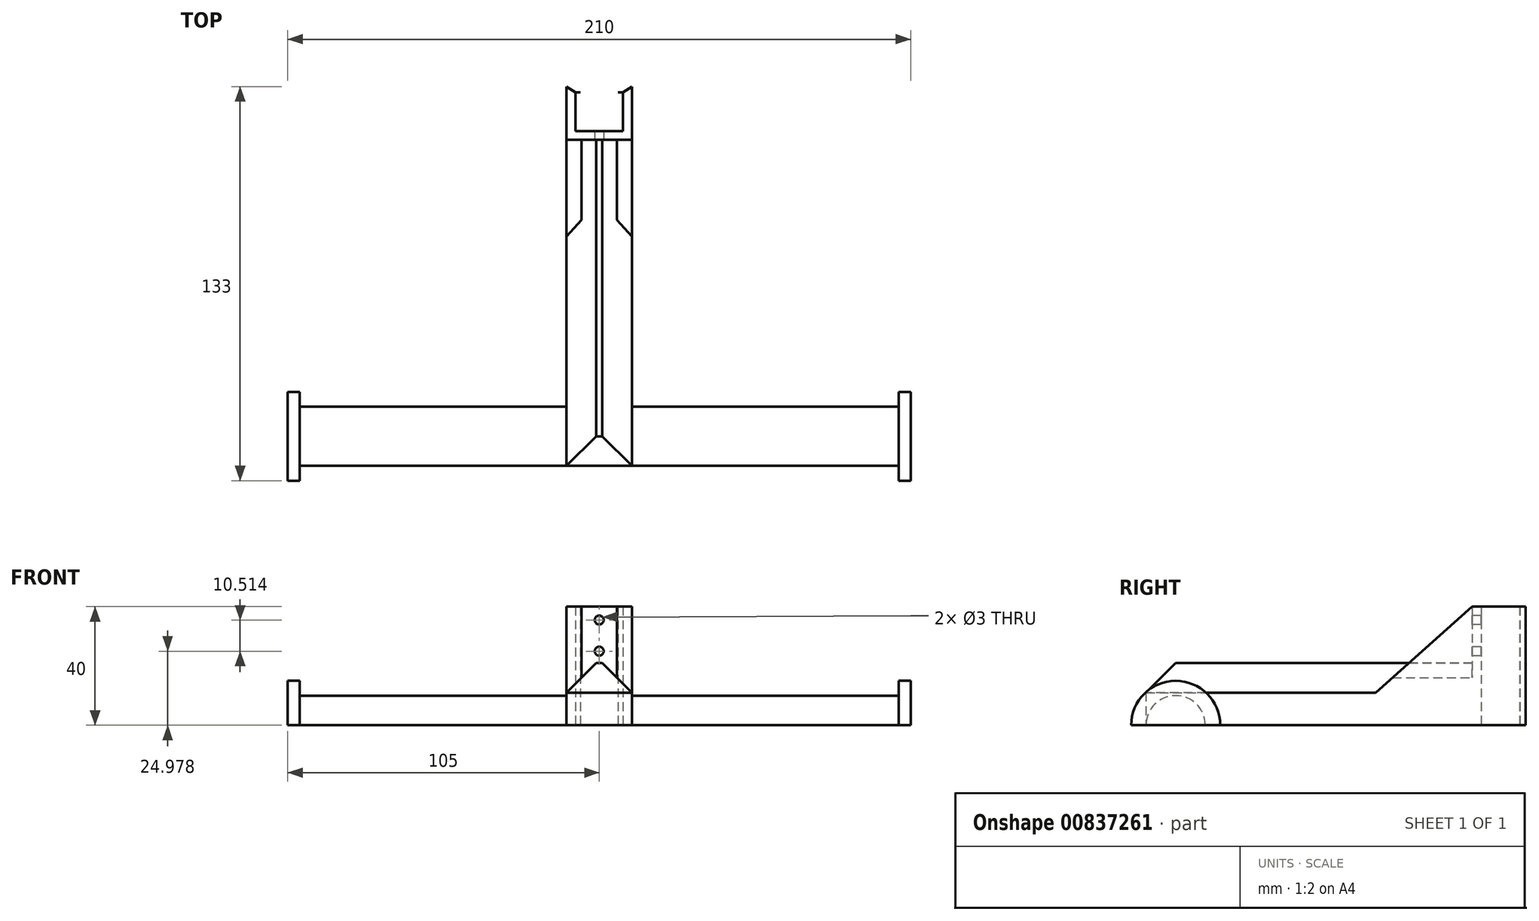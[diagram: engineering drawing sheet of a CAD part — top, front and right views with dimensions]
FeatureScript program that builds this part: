
annotation { "Feature Type Name" : "Feature", "Feature Type Description" : "" }
export const myFeature = defineFeature(function(context is Context, id is Id, definition is map)
    precondition{}
    {
        {
            var Q0;
            Q0=qCreatedBy(makeId("Front.planeOp"),FACE);
            var sketch = newSketch(context, id + "F0", { "sketchPlane" : qUnion([Q0])});
            skLineSegment(sketch, "E0.bottom", {"start": v(8, 7.5) * mm, "end": v(-8, 7.5) * mm});
            skLineSegment(sketch, "E0.top", {"start": v(8, -7.5) * mm, "end": v(-8, -7.5) * mm});
            skLineSegment(sketch, "E0.left", {"start": v(8, 7.5) * mm, "end": v(8, -7.5) * mm});
            skLineSegment(sketch, "E0.right", {"start": v(-8, 7.5) * mm, "end": v(-8, -7.5) * mm});
            skPoint(sketch, "E0.middle", {"position": v(0, 0) * mm});
            skLineSegment(sketch, "E1", {"start": v(8, 5.5) * mm, "end": v(6.3, 5.5) * mm});
            skLineSegment(sketch, "E2", {"start": v(6.3, 5.5) * mm, "end": v(8, 5.53) * mm});
            skLineSegment(sketch, "E3.0", {"start": v(11, 10.5) * mm, "end": v(-11, 10.5) * mm});
            skLineSegment(sketch, "E3.1", {"start": v(11, 10.5) * mm, "end": v(11, -10.5) * mm});
            skLineSegment(sketch, "E3.2", {"start": v(11, -10.5) * mm, "end": v(-11, -10.5) * mm});
            skLineSegment(sketch, "E3.3", {"start": v(-11, 10.5) * mm, "end": v(-11, -10.5) * mm});
            skLineSegment(sketch, "E4.MirrorCS", {"start": v(-6.3, 5.5) * mm, "end": v(-8, 5.53) * mm});
            skLineSegment(sketch, "E5.MirrorCS", {"start": v(-8, 5.5) * mm, "end": v(-6.3, 5.5) * mm});
            skLineSegment(sketch, "E6", {"start": v(8, 7.5) * mm, "end": v(11, 7.5) * mm});
            skLineSegment(sketch, "E7.MirrorCS", {"start": v(-8, 7.5) * mm, "end": v(-11, 7.5) * mm});
            skLineSegment(sketch, "E8", {"start": v(8, 5.53) * mm, "end": v(11, 7.5) * mm});
            skLineSegment(sketch, "E9.MirrorCS", {"start": v(-8, 5.53) * mm, "end": v(-11, 7.5) * mm});
            skSolve(sketch);
        }
        {
            var Q0;
            {var subQ1=sQuery(id+"F0.wireOp",EDGE,"E0.top");Q0=makeQuery(id+"F0.imprint","IMPRINT",FACE,{"disambiguationData":[TD([[makeQuery(id+"F0.imprint","IMPRINT",EDGE,{"derivedFrom":subQ1}),1.0]])]});}
            var Q1;
            {var subQ0=sQuery(id+"F0.wireOp",EDGE,"E4.MirrorCS");Q1=makeQuery(id+"F0.imprint","IMPRINT",FACE,{"disambiguationData":[TD([[makeQuery(id+"F0.imprint","IMPRINT",EDGE,{"derivedFrom":subQ0}),1.0]])]});}
            var Q2;
            {var subQ0=sQuery(id+"F0.wireOp",EDGE,"E1");Q2=makeQuery(id+"F0.imprint","IMPRINT",FACE,{"disambiguationData":[TD([[makeQuery(id+"F0.imprint","IMPRINT",EDGE,{"derivedFrom":subQ0}),-1.0]])]});}
            extrude(context, id + "F1", {"entities" : qUnion([Q0, Q1, Q2]), "depth" : 40 * mm, "offsetDistance" : 25 * mm});
        }
        {
            var Q0;
            Q0=makeQuery(id+"F1.opExtrude","SWEPT_FACE",FACE,{"disambiguationData":[OSD([sQuery(id+"F0.wireOp",EDGE,"E3.2")])]});
            var sketch = newSketch(context, id + "F2", { "sketchPlane" : qUnion([Q0])});
            skLineSegment(sketch, "E10", {"start": v(-11, 21) * mm, "end": v(11, 21) * mm});
            skSolve(sketch);
        }
        {
            var Q0;
            {var subQ0=sQuery(id+"F2.wireOp",EDGE,"E10");Q0=makeQuery(id+"F2.imprint","IMPRINT",FACE,{"disambiguationData":[TD([[makeQuery(id+"F2.imprint","IMPRINT",EDGE,{"derivedFrom":subQ0}),-1.0]])]});}
            extrude(context, id + "F3", {"entities" : qUnion([Q0]), "operationType" : NewBodyOperationType.ADD, "depth" : 110 * mm, "offsetDistance" : 25 * mm});
        }
        {
            var Q0;
            {var subQ0=sQuery(id+"F0.wireOp",EDGE,"E3.3");Q0=makeQuery(id+"F3.boolean.opBoolean","MERGE",FACE,{"derivedFrom":[makeQuery(id+"F1.opExtrude","SWEPT_FACE",FACE,{"disambiguationData":[OSD([subQ0])]}),makeQuery(id+"F3.opExtrude","SWEPT_FACE",FACE,{"disambiguationData":[OSD([sQuery(id+"F0.wireOp",EDGE,"E3.2"),subQ0])]})]});}
            var sketch = newSketch(context, id + "F4", { "sketchPlane" : qUnion([Q0])});
            skLineSegment(sketch, "E11", {"start": v(40, -10.5) * mm, "end": v(21, -31.83) * mm});
            skSolve(sketch);
        }
        {
            var Q0;
            {var subQ0=sQuery(id+"F4.wireOp",EDGE,"E11");Q0=makeQuery(id+"F4.imprint","IMPRINT",FACE,{"disambiguationData":[TD([[makeQuery(id+"F4.imprint","IMPRINT",EDGE,{"derivedFrom":subQ0}),-1.0]])]});}
            extrude(context, id + "F5", {"entities" : qUnion([Q0]), "operationType" : NewBodyOperationType.ADD, "depth" : -5 * mm, "offsetDistance" : 25 * mm});
        }
        {
            var Q0;
            Q0=makeQuery(id+"F1.opExtrude","SWEPT_BODY",BODY,{"disambiguationData":[OSD([sQuery(id+"F0.wireOp",EDGE,"E0.top"),sQuery(id+"F0.wireOp",EDGE,"E0.left"),sQuery(id+"F0.wireOp",EDGE,"E0.right"),sQuery(id+"F0.wireOp",EDGE,"E1"),sQuery(id+"F0.wireOp",EDGE,"E2"),sQuery(id+"F0.wireOp",EDGE,"E3.1"),sQuery(id+"F0.wireOp",EDGE,"E3.2"),sQuery(id+"F0.wireOp",EDGE,"E3.3"),sQuery(id+"F0.wireOp",EDGE,"E4.MirrorCS"),sQuery(id+"F0.wireOp",EDGE,"E5.MirrorCS"),sQuery(id+"F0.wireOp",EDGE,"E8"),sQuery(id+"F0.wireOp",EDGE,"E9.MirrorCS")])]});
            var Q1;
            Q1=qCreatedBy(makeId("Right.planeOp"),FACE);
            mirror(context, id + "F6", {"operationType" : NewBodyOperationType.ADD, "entities" : qUnion([Q0]), "mirrorPlane" : qUnion([Q1])});
        }
        {
            var Q0;
            Q0=makeQuery(id+"F3.opExtrude","SWEPT_EDGE",EDGE,{"disambiguationData":[OSD([sQuery(id+"F0.wireOp",EDGE,"E3.2"),sQuery(id+"F0.wireOp",EDGE,"E3.3"),sQuery(id+"F2.wireOp",EDGE,"E10")])]});
            var Q1;
            Q1=makeQuery(id+"F3.opExtrude","CAP_EDGE",EDGE,{"disambiguationData":[OSD([sQuery(id+"F2.wireOp",EDGE,"E10")])],"isStart":false});
            var Q2;
            Q2=makeQuery(id+"F3.opExtrude","SWEPT_EDGE",EDGE,{"disambiguationData":[OSD([sQuery(id+"F0.wireOp",EDGE,"E3.1"),sQuery(id+"F0.wireOp",EDGE,"E3.2"),sQuery(id+"F2.wireOp",EDGE,"E10")])]});
            chamfer(context, id + "F7", {"entities" : qUnion([Q0, Q1, Q2]), "width" : 10 * mm, "tangentPropagation" : true});
        }
        {
            var Q0;
            {var subQ0=sQuery(id+"F0.wireOp",EDGE,"E3.3");var subQ1=sQuery(id+"F0.wireOp",EDGE,"E3.2");Q0=makeQuery(id+"F5.boolean.opBoolean","MERGE",FACE,{"derivedFrom":[makeQuery(id+"F3.boolean.opBoolean","MERGE",FACE,{"derivedFrom":[makeQuery(id+"F1.opExtrude","SWEPT_FACE",FACE,{"disambiguationData":[OSD([subQ0])]}),makeQuery(id+"F3.opExtrude","SWEPT_FACE",FACE,{"disambiguationData":[OSD([subQ1,subQ0])]})]}),makeQuery(id+"F5.opExtrude","CAP_FACE",FACE,{"disambiguationData":[OSD([subQ1,subQ0,sQuery(id+"F2.wireOp",EDGE,"E10"),sQuery(id+"F4.wireOp",EDGE,"E11")])],"isStart":true})]});}
            var sketch = newSketch(context, id + "F8", { "sketchPlane" : qUnion([Q0])});
            skPoint(sketch, "E12", {"position": v(0, -110.5) * mm});
            skPoint(sketch, "E13", {"position": v(0, -120.5) * mm});
            skCircle(sketch, "E14", {"center": v(0, -110.5) * mm, "radius": 10 * mm});
            skPoint(sketch, "E15", {"position": v(0, -100.5) * mm});
            skSolve(sketch);
        }
        {
            var Q0;
            {var subQ0=sQuery(id+"F8.wireOp",EDGE,"E14");var subQ1=sQuery(id+"F0.wireOp",EDGE,"E3.3");var subQ2=sQuery(id+"F0.wireOp",EDGE,"E3.2");var subQ3=makeQuery(id+"F3.boolean.opBoolean","MERGE",EDGE,{"derivedFrom":[makeQuery(id+"F1.opExtrude","CAP_EDGE",EDGE,{"disambiguationData":[OSD([subQ1])],"isStart":true}),makeQuery(id+"F3.opExtrude","SWEPT_EDGE",EDGE,{"disambiguationData":[OSD([subQ2,subQ1])]})]});var subQ5=makeQuery(id+"F8.imprint","INTERSECT",VERTEX,{"derivedFrom":[subQ3,subQ0]});Q0=makeQuery(id+"F8.imprint","IMPRINT",FACE,{"disambiguationData":[TD([[makeQuery(id+"F8.imprint","IMPRINT",EDGE,{"disambiguationData":[TD([[subQ5,1.0]])],"derivedFrom":subQ0}),1.0]])]});}
            extrude(context, id + "F9", {"entities" : qUnion([Q0]), "operationType" : NewBodyOperationType.ADD, "depth" : 90 * mm, "offsetDistance" : 25 * mm});
        }
        {
            var Q0;
            Q0=makeQuery(id+"F9.opExtrude","CAP_FACE",FACE,{"disambiguationData":[OSD([sQuery(id+"F0.wireOp",EDGE,"E3.2"),sQuery(id+"F0.wireOp",EDGE,"E3.3"),sQuery(id+"F8.wireOp",EDGE,"E14")])],"isStart":false});
            var sketch = newSketch(context, id + "F10", { "sketchPlane" : qUnion([Q0])});
            skCircle(sketch, "E16", {"center": v(0, -110.5) * mm, "radius": 15 * mm});
            skPoint(sketch, "E17", {"position": v(0, -125.5) * mm});
            skLineSegment(sketch, "E18", {"start": v(0, -95.5) * mm, "end": v(0, -120.5) * mm});
            skLineSegment(sketch, "E19", {"start": v(0, -95.5) * mm, "end": v(0, -125.5) * mm});
            skSolve(sketch);
        }
        {
            var Q0;
            {var subQ4=makeQuery(id+"F9.opExtrude","CAP_EDGE",EDGE,{"disambiguationData":[OSD([sQuery(id+"F8.wireOp",EDGE,"E14")])],"isStart":false});Q0=makeQuery(id+"F10.imprint","IMPRINT",FACE,{"disambiguationData":[TD([[makeQuery(id+"F10.imprint","IMPRINT",EDGE,{"derivedFrom":subQ4}),-1.0]])]});}
            var Q1;
            {var subQ1=makeQuery(id+"F9.opExtrude","CAP_EDGE",EDGE,{"disambiguationData":[OSD([sQuery(id+"F8.wireOp",EDGE,"E14")])],"isStart":false});Q1=makeQuery(id+"F10.imprint","IMPRINT",FACE,{"disambiguationData":[TD([[makeQuery(id+"F10.imprint","IMPRINT",EDGE,{"derivedFrom":subQ1}),1.0]])]});}
            extrude(context, id + "F11", {"entities" : qUnion([Q0, Q1]), "operationType" : NewBodyOperationType.ADD, "depth" : 4 * mm, "offsetDistance" : 25 * mm});
        }
        {
            var Q0;
            Q0=makeQuery(id+"F1.opExtrude","SWEPT_BODY",BODY,{"disambiguationData":[OSD([sQuery(id+"F0.wireOp",EDGE,"E0.top"),sQuery(id+"F0.wireOp",EDGE,"E0.left"),sQuery(id+"F0.wireOp",EDGE,"E0.right"),sQuery(id+"F0.wireOp",EDGE,"E1"),sQuery(id+"F0.wireOp",EDGE,"E2"),sQuery(id+"F0.wireOp",EDGE,"E3.1"),sQuery(id+"F0.wireOp",EDGE,"E3.2"),sQuery(id+"F0.wireOp",EDGE,"E3.3"),sQuery(id+"F0.wireOp",EDGE,"E4.MirrorCS"),sQuery(id+"F0.wireOp",EDGE,"E5.MirrorCS"),sQuery(id+"F0.wireOp",EDGE,"E8"),sQuery(id+"F0.wireOp",EDGE,"E9.MirrorCS")])]});
            var Q1;
            Q1=qCreatedBy(makeId("Right.planeOp"),FACE);
            mirror(context, id + "F12", {"operationType" : NewBodyOperationType.ADD, "entities" : qUnion([Q0]), "mirrorPlane" : qUnion([Q1])});
        }
        {
            var Q0;
            Q0=makeQuery(id+"F1.opExtrude","SWEPT_FACE",FACE,{"disambiguationData":[OSD([sQuery(id+"F0.wireOp",EDGE,"E3.2")])]});
            var sketch = newSketch(context, id + "F13", { "sketchPlane" : qUnion([Q0])});
            skPoint(sketch, "E20", {"position": v(0, 24.98) * mm});
            skPoint(sketch, "E21", {"position": v(0, 35.5) * mm});
            skSolve(sketch);
        }
        {
            var Q0;
            Q0=sQuery(id+"F13.wireOp",VERTEX,"E21");
            var Q1;
            Q1=sQuery(id+"F13.wireOp",VERTEX,"E20");
            var Q2;
            Q2=makeQuery(id+"F1.opExtrude","SWEPT_BODY",BODY,{"disambiguationData":[OSD([sQuery(id+"F0.wireOp",EDGE,"E0.top"),sQuery(id+"F0.wireOp",EDGE,"E0.left"),sQuery(id+"F0.wireOp",EDGE,"E0.right"),sQuery(id+"F0.wireOp",EDGE,"E1"),sQuery(id+"F0.wireOp",EDGE,"E2"),sQuery(id+"F0.wireOp",EDGE,"E3.1"),sQuery(id+"F0.wireOp",EDGE,"E3.2"),sQuery(id+"F0.wireOp",EDGE,"E3.3"),sQuery(id+"F0.wireOp",EDGE,"E4.MirrorCS"),sQuery(id+"F0.wireOp",EDGE,"E5.MirrorCS"),sQuery(id+"F0.wireOp",EDGE,"E8"),sQuery(id+"F0.wireOp",EDGE,"E9.MirrorCS")])]});
            hole(context, id + "F14", {"style" : HoleStyle.SIMPLE, "endStyle" : HoleEndStyle.BLIND, "holeDiameter" : 3 * mm, "majorDiameter" : 5 * mm, "holeDepth" : 4 * mm, "isTappedThrough" : true, "tappedDepth" : 12 * mm, "tapClearance" : 3, "locations" : qUnion([Q0, Q1]), "scope" : qUnion([Q2])});
        }
        {
            var Q0;
            {var subQ0=sQuery(id+"F0.wireOp",EDGE,"E3.3");var subQ1=sQuery(id+"F0.wireOp",EDGE,"E3.2");var subQ2=makeQuery(id+"F11.boolean.opBoolean","MERGE",FACE,{"derivedFrom":[makeQuery(id+"F9.boolean.opBoolean","MERGE",FACE,{"derivedFrom":[makeQuery(id+"F3.boolean.opBoolean","MERGE",FACE,{"derivedFrom":[makeQuery(id+"F1.opExtrude","CAP_FACE",FACE,{"disambiguationData":[OSD([sQuery(id+"F0.wireOp",EDGE,"E0.top"),sQuery(id+"F0.wireOp",EDGE,"E0.left"),sQuery(id+"F0.wireOp",EDGE,"E0.right"),sQuery(id+"F0.wireOp",EDGE,"E1"),sQuery(id+"F0.wireOp",EDGE,"E2"),sQuery(id+"F0.wireOp",EDGE,"E3.1"),subQ1,subQ0,sQuery(id+"F0.wireOp",EDGE,"E4.MirrorCS"),sQuery(id+"F0.wireOp",EDGE,"E5.MirrorCS"),sQuery(id+"F0.wireOp",EDGE,"E8"),sQuery(id+"F0.wireOp",EDGE,"E9.MirrorCS")])],"isStart":true}),makeQuery(id+"F3.opExtrude","SWEPT_FACE",FACE,{"disambiguationData":[OSD([subQ1])]})]}),makeQuery(id+"F9.opExtrude","SWEPT_FACE",FACE,{"disambiguationData":[OSD([subQ1,subQ0])]})]}),makeQuery(id+"F11.opExtrude","SWEPT_FACE",FACE,{"disambiguationData":[OSD([sQuery(id+"F10.wireOp",EDGE,"E19")])]})]});Q0=makeQuery(id+"F12.boolean.opBoolean","MERGE",FACE,{"derivedFrom":[subQ2,makeQuery(id+"F12.opPattern","COPY",FACE,{"derivedFrom":subQ2,"instanceName":"1"})]});}
            var sketch = newSketch(context, id + "F15", { "sketchPlane" : qUnion([Q0])});
            skLineSegment(sketch, "E22", {"start": v(-8, 0) * mm, "end": v(8, 0) * mm});
            skSolve(sketch);
        }
        {
            var Q0;
            Q0=makeQuery(id+"F1.opExtrude","SWEPT_BODY",BODY,{"disambiguationData":[OSD([sQuery(id+"F0.wireOp",EDGE,"E0.top"),sQuery(id+"F0.wireOp",EDGE,"E0.left"),sQuery(id+"F0.wireOp",EDGE,"E0.right"),sQuery(id+"F0.wireOp",EDGE,"E1"),sQuery(id+"F0.wireOp",EDGE,"E2"),sQuery(id+"F0.wireOp",EDGE,"E3.1"),sQuery(id+"F0.wireOp",EDGE,"E3.2"),sQuery(id+"F0.wireOp",EDGE,"E3.3"),sQuery(id+"F0.wireOp",EDGE,"E4.MirrorCS"),sQuery(id+"F0.wireOp",EDGE,"E5.MirrorCS"),sQuery(id+"F0.wireOp",EDGE,"E8"),sQuery(id+"F0.wireOp",EDGE,"E9.MirrorCS")])]});
            var Q1;
            Q1=sQuery(id+"F15.wireOp",EDGE,"E22");
            transform(context, id + "F16", {"entities" : qUnion([Q0]), "transformType" : TransformType.ROTATION, "transformAxis" : qUnion([Q1]), "angle" : 90 * degree, "makeCopy" : false});
        }
    });
